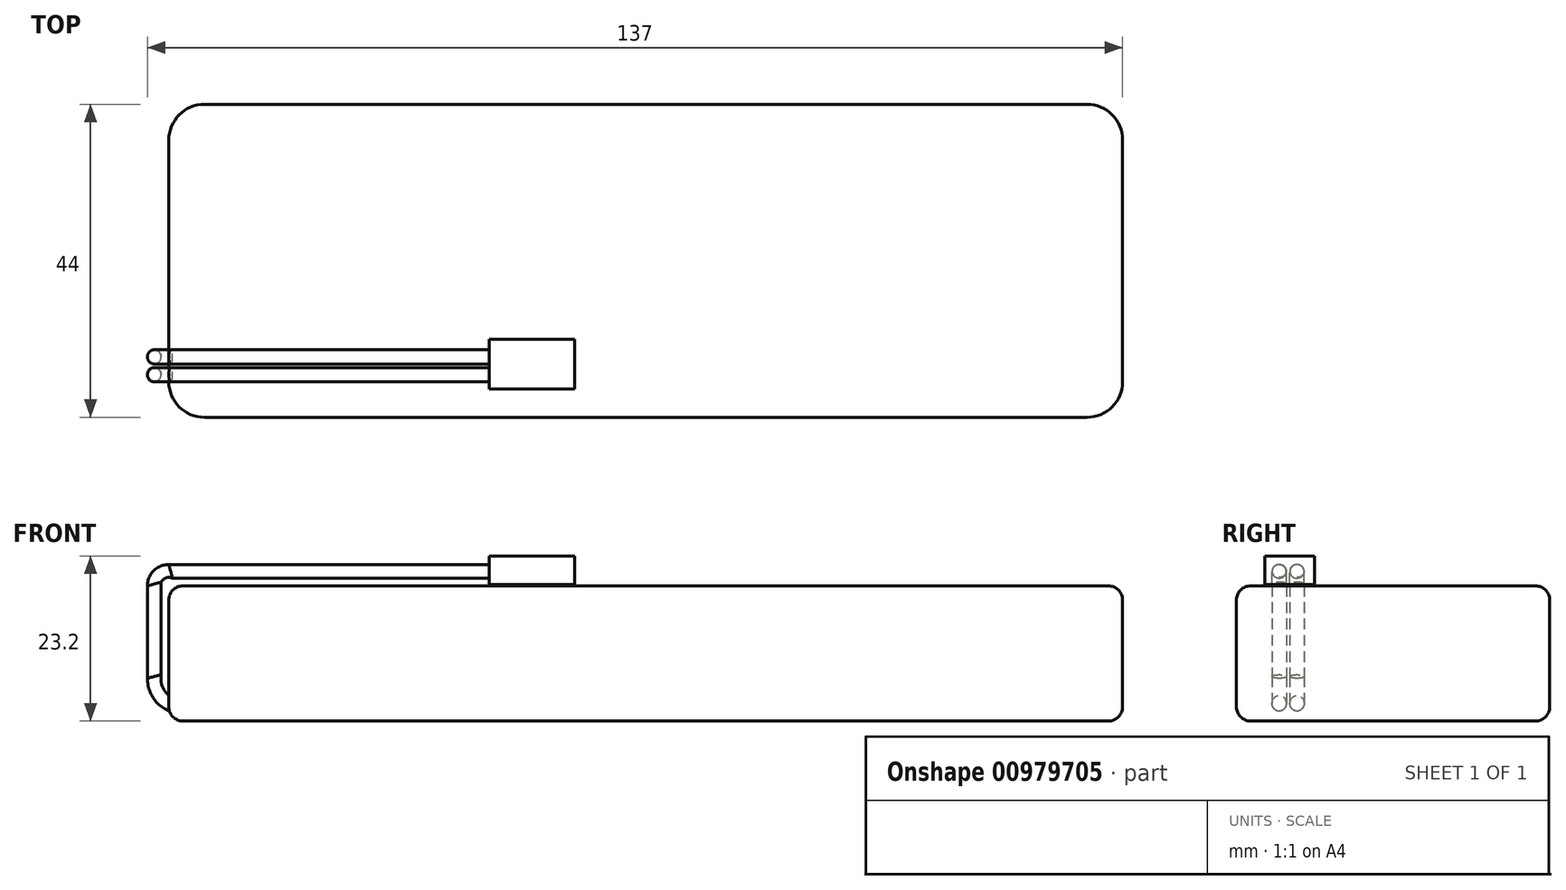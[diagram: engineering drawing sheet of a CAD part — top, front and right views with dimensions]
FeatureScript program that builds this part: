
annotation { "Feature Type Name" : "Feature", "Feature Type Description" : "" }
export const myFeature = defineFeature(function(context is Context, id is Id, definition is map)
    precondition{}
    {
        {
            var Q0;
            Q0=qCreatedBy(makeId("Top.planeOp"),FACE);
            var sketch = newSketch(context, id + "F0", { "sketchPlane" : qUnion([Q0])});
            skLineSegment(sketch, "E0.bottom", {"start": v(0, 0) * mm, "end": v(134, 0) * mm});
            skLineSegment(sketch, "E0.top", {"start": v(0, 44) * mm, "end": v(134, 44) * mm});
            skLineSegment(sketch, "E0.left", {"start": v(0, 0) * mm, "end": v(0, 44) * mm});
            skLineSegment(sketch, "E0.right", {"start": v(134, 0) * mm, "end": v(134, 44) * mm});
            skSolve(sketch);
        }
        {
            var Q0;
            Q0 = qSketchRegion(id + "F0", true);
            extrude(context, id + "F1", {"entities" : qUnion([Q0]), "depth" : 19 * mm, "offsetDistance" : 25 * mm});
        }
        {
            var Q0;
            Q0=makeQuery(id+"F1.opExtrude","SWEPT_EDGE",EDGE,{"disambiguationData":[OSD([sQuery(id+"F0.wireOp",EDGE,"E0.bottom"),sQuery(id+"F0.wireOp",EDGE,"E0.left")])]});
            var Q1;
            Q1=makeQuery(id+"F1.opExtrude","SWEPT_EDGE",EDGE,{"disambiguationData":[OSD([sQuery(id+"F0.wireOp",EDGE,"E0.bottom"),sQuery(id+"F0.wireOp",EDGE,"E0.right")])]});
            var Q2;
            Q2=makeQuery(id+"F1.opExtrude","SWEPT_EDGE",EDGE,{"disambiguationData":[OSD([sQuery(id+"F0.wireOp",EDGE,"E0.top"),sQuery(id+"F0.wireOp",EDGE,"E0.right")])]});
            var Q3;
            Q3=makeQuery(id+"F1.opExtrude","SWEPT_EDGE",EDGE,{"disambiguationData":[OSD([sQuery(id+"F0.wireOp",EDGE,"E0.top"),sQuery(id+"F0.wireOp",EDGE,"E0.left")])]});
            fillet(context, id + "F2", {"entities" : qUnion([Q0, Q1, Q2, Q3]), "tangentPropagation" : true, "radius" : 5 * mm, "defaultsChanged" : false, "vertexSettings" : [], "allowEdgeOverflow" : false});
        }
        {
            var Q0;
            Q0=makeQuery(id+"F1.opExtrude","CAP_EDGE",EDGE,{"disambiguationData":[OSD([sQuery(id+"F0.wireOp",EDGE,"E0.top")])],"isStart":false});
            var Q1;
            Q1=makeQuery(id+"F1.opExtrude","CAP_EDGE",EDGE,{"disambiguationData":[OSD([sQuery(id+"F0.wireOp",EDGE,"E0.top")])],"isStart":true});
            fillet(context, id + "F3", {"entities" : qUnion([Q0, Q1]), "tangentPropagation" : true, "radius" : 2 * mm, "defaultsChanged" : true, "vertexSettings" : [], "allowEdgeOverflow" : false});
        }
        {
            var Q0;
            Q0=qCreatedBy(makeId("Front.planeOp"),FACE);
            var sketch = newSketch(context, id + "F4", { "sketchPlane" : qUnion([Q0])});
            skPoint(sketch, "E1.end.orphan", {"position": v(5, 0) * mm});
            skArc(sketch, "E2", {"start": v(-3, 6) * mm, "mid": v(-1.97, 2.96) * mm, "end": v(0.69, 1.18) * mm});
            skLineSegment(sketch, "E3", {"start": v(-3, 6) * mm, "end": v(-3, 19) * mm});
            skArc(sketch, "E4", {"start": v(0, 22) * mm, "mid": v(-2.12, 21.12) * mm, "end": v(-3, 19) * mm});
            skLineSegment(sketch, "E5", {"start": v(0.69, 1.18) * mm, "end": v(5, 0) * mm});
            skLineSegment(sketch, "E6", {"start": v(0, 22) * mm, "end": v(45, 22) * mm});
            skSolve(sketch);
        }
        {
            var Q0;
            Q0=qCreatedBy(makeId("Right.planeOp"),FACE);
            cPlane(context, id + "F5", {"entities" : qUnion([Q0]), "cplaneType" : CPlaneType.OFFSET, "offset" : 5 * mm, "width" : 150 * mm, "height" : 150 * mm});
        }
        {
            var Q0;
            Q0=qCreatedBy(id+"F5.planeOp",FACE);
            var sketch = newSketch(context, id + "F6", { "sketchPlane" : qUnion([Q0])});
            skCircle(sketch, "E7", {"center": v(6, 1) * mm, "radius": 1 * mm});
            skCircle(sketch, "E8", {"center": v(8.5, 1) * mm, "radius": 1 * mm});
            skSolve(sketch);
        }
        {
            var Q0;
            Q0 = qSketchRegion(id + "F6", true);
            var Q1;
            Q1 = qConstructionFilter(qBodyType(qCreatedBy(id + "F4" ,EDGE), BodyType.WIRE), ConstructionObject.NO);
            sweep(context, id + "F7", {"operationType" : NewBodyOperationType.ADD, "profiles" : qUnion([Q0]), "path" : qUnion([Q1])});
        }
        {
            var Q0;
            Q0=qCreatedBy(makeId("Right.planeOp"),FACE);
            cPlane(context, id + "F8", {"entities" : qUnion([Q0]), "cplaneType" : CPlaneType.OFFSET, "offset" : 45 * mm, "width" : 150 * mm, "height" : 150 * mm});
        }
        {
            var Q0;
            Q0=qCreatedBy(id+"F8.planeOp",FACE);
            var sketch = newSketch(context, id + "F9", { "sketchPlane" : qUnion([Q0])});
            skLineSegment(sketch, "E9.bottom", {"start": v(3.98, 23.2) * mm, "end": v(10.98, 23.2) * mm});
            skLineSegment(sketch, "E9.top", {"start": v(3.98, 19.2) * mm, "end": v(10.98, 19.2) * mm});
            skLineSegment(sketch, "E9.left", {"start": v(3.98, 23.2) * mm, "end": v(3.98, 19.2) * mm});
            skLineSegment(sketch, "E9.right", {"start": v(10.98, 23.2) * mm, "end": v(10.98, 19.2) * mm});
            skSolve(sketch);
        }
        {
            var Q0;
            Q0 = qSketchRegion(id + "F9", true);
            extrude(context, id + "F10", {"entities" : qUnion([Q0]), "operationType" : NewBodyOperationType.ADD, "depth" : 12 * mm, "offsetDistance" : 25 * mm});
        }
    });
